# Revit family: xBasin-Undercounter-DXV-Pop_Grande-D20140000.415
name_source: partatom
category: Plumbing Fixtures
revit_build: Autodesk Revit 2014 (Build: 20130308_1515(x64)
units: mm (PartAtom-declared; Revit-internal decimal feet)

## types (1)
- D20140000.415
    ADA Compliant = Yes
    Assembly Code = D2010310
    Basin Shape = Rectangular
    CW Connection = Yes
    CWFU = 1.5
    Cold Water Connection Diameter = 1/2"
    Cold Water Connection Height = 22 3/4"
    Cold Water Connection Radius = 1/4"
    Cold Water Connection Width = 4"
    Default Elevation = 34"
    Description = Pop Grande Rectangle Under Counter Lavatory
    Finish = Vitreous China-DXV-415-Canvas White
    HW Connection = Yes
    HWFU = 1.5
    Height = 7 1/2"
    Hot Water Connection Diameter = 1/2"
    Hot Water Connection Height = 22 3/4"
    Hot Water Connection Radius = 1/4"
    Hot Water Connection Width = 4"
    Installation Type = Undercounter
    Length = 16 5/8"
    Manufacturer = DXV
    Material = Vitreous China-DXV-415-Canvas White
    Model = D20140000.415
    Outlet Location = 3 1/16"
    Price = Prices may vary. Please consult Manufacturer Representative for most up-to-date price list.
    Product Documentation Link = https://dxv01.blob.core.windows.net
    Product Page URL = https://www.dxv.com
    URL = http://www.dxv.com
    Vent Connection = No
    WFU = 2
    Warranty Documentation Link = https://www.dxv.com
    Waste Connection = Yes
    Waste Connection Diameter = 1 1/4"
    Waste Connection Height = 20 1/4"
    Waste Connection Radius = 5/8"
    Width = 23 5/8"

## geometry (parser evidence)
native form markers: Sweep x1
no freeform markers — native parametric forms only
